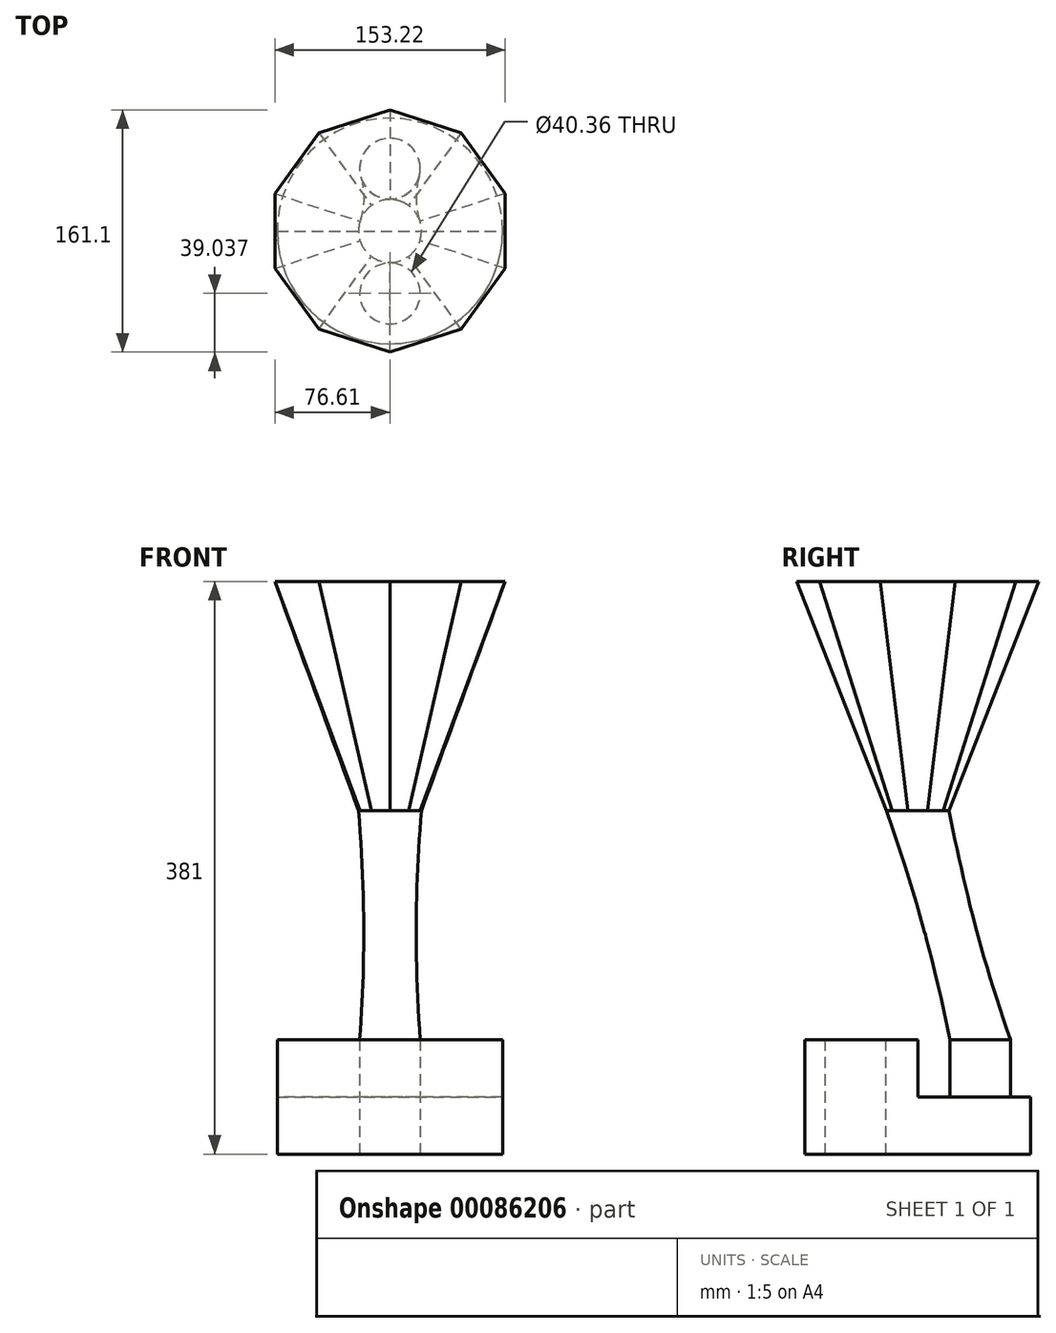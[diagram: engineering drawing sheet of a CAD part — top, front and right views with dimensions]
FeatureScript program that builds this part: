
annotation { "Feature Type Name" : "Feature", "Feature Type Description" : "" }
export const myFeature = defineFeature(function(context is Context, id is Id, definition is map)
    precondition{}
    {
        {
            var Q0;
            Q0=qCreatedBy(makeId("Top.planeOp"),FACE);
            var sketch = newSketch(context, id + "F0", { "sketchPlane" : qUnion([Q0])});
            skCircle(sketch, "E0", {"center": v(0, 0) * mm, "radius": 75.02 * mm});
            skLineSegment(sketch, "E1", {"start": v(-75.02, 0) * mm, "end": v(75.02, 0) * mm});
            skCircle(sketch, "E2", {"center": v(0, 41.51) * mm, "radius": 20.18 * mm});
            skCircle(sketch, "E3.MirrorC", {"center": v(0, -41.51) * mm, "radius": 20.18 * mm});
            skSolve(sketch);
        }
        {
            var Q0;
            {var subQ0=sQuery(id+"F0.wireOp",EDGE,"E1");Q0=makeQuery(id+"F0.imprint","IMPRINT",FACE,{"disambiguationData":[TD([[makeQuery(id+"F0.imprint","IMPRINT",EDGE,{"derivedFrom":subQ0}),1.0]])]});}
            extrude(context, id + "F1", {"entities" : qUnion([Q0]), "depth" : 38.1 * mm});
        }
        {
            var Q0;
            {var subQ0=sQuery(id+"F0.wireOp",EDGE,"E1");Q0=makeQuery(id+"F0.imprint","IMPRINT",FACE,{"disambiguationData":[TD([[makeQuery(id+"F0.imprint","IMPRINT",EDGE,{"derivedFrom":subQ0}),-1.0]])]});}
            extrude(context, id + "F2", {"entities" : qUnion([Q0]), "operationType" : NewBodyOperationType.ADD, "depth" : 25.4 * mm});
        }
        {
            var Q0;
            Q0=makeQuery(id+"F0.imprint","IMPRINT",FACE,{"disambiguationData":[TD([[makeQuery(id+"F0.imprint","IMPRINT",EDGE,{"derivedFrom":sQuery(id+"F0.wireOp",EDGE,"E3.MirrorC")}),-1.0]])]});
            var Q1;
            Q1=makeQuery(id+"F0.imprint","IMPRINT",FACE,{"disambiguationData":[TD([[makeQuery(id+"F0.imprint","IMPRINT",EDGE,{"derivedFrom":sQuery(id+"F0.wireOp",EDGE,"E2")}),1.0]])]});
            extrude(context, id + "F3", {"entities" : qUnion([Q0, Q1]), "operationType" : NewBodyOperationType.ADD, "depth" : 76.2 * mm});
        }
        {
            var Q0;
            Q0=makeQuery(id+"F3.opExtrude","CAP_FACE",FACE,{"disambiguationData":[OSD([sQuery(id+"F0.wireOp",EDGE,"E3.MirrorC")])],"isStart":false});
            cPlane(context, id + "F4", {"entities" : qUnion([Q0]), "cplaneType" : CPlaneType.OFFSET, "offset" : 152.4 * mm, "width" : 152.4 * mm, "height" : 152.4 * mm});
        }
        {
            var Q0;
            Q0=qCreatedBy(id+"F4.planeOp",FACE);
            var sketch = newSketch(context, id + "F5", { "sketchPlane" : qUnion([Q0])});
            skCircle(sketch, "E4", {"center": v(0, 0) * mm, "radius": 20.94 * mm});
            skSolve(sketch);
        }
        {
            var Q0;
            Q0=makeQuery(id+"F3.opExtrude","CAP_FACE",FACE,{"disambiguationData":[OSD([sQuery(id+"F0.wireOp",EDGE,"E2")])],"isStart":false});
            var Q1;
            Q1=makeQuery(id+"F5.imprint","IMPRINT",FACE,{"disambiguationData":[TD([[makeQuery(id+"F5.imprint","IMPRINT",EDGE,{"derivedFrom":sQuery(id+"F5.wireOp",EDGE,"E4")}),1.0]])]});
            loft(context, id + "F6", {"sheetProfilesArray" : [{ "sheetProfileEntities" : qUnion([Q0]) }, { "sheetProfileEntities" : qUnion([Q1]) }]});
        }
        {
            var Q0;
            Q0=makeQuery(id+"F6.opLoft","CAP_FACE",FACE,{"disambiguationData":[OSD([makeQuery(id+"F5.imprint","IMPRINT",FACE,{"disambiguationData":[TD([[makeQuery(id+"F5.imprint","IMPRINT",EDGE,{"derivedFrom":sQuery(id+"F5.wireOp",EDGE,"E4")}),1.0]])]})])],"isStart":true});
            cPlane(context, id + "F7", {"entities" : qUnion([Q0]), "cplaneType" : CPlaneType.OFFSET, "offset" : 152.4 * mm, "width" : 152.4 * mm, "height" : 152.4 * mm});
        }
        {
            var Q0;
            Q0=qCreatedBy(id+"F7.planeOp",FACE);
            var sketch = newSketch(context, id + "F8", { "sketchPlane" : qUnion([Q0])});
            skCircle(sketch, "E5.cCircle", {"center": v(0, 0) * mm, "radius": 76.6 * mm, "construction": true});
            skLineSegment(sketch, "E5.0", {"start": v(76.6, 24.9) * mm, "end": v(76.6, -24.9) * mm});
            skLineSegment(sketch, "E5.1", {"start": v(76.6, -24.9) * mm, "end": v(47.35, -65.17) * mm});
            skLineSegment(sketch, "E5.2", {"start": v(47.35, -65.17) * mm, "end": v(0, -80.55) * mm});
            skLineSegment(sketch, "E5.3", {"start": v(0, -80.55) * mm, "end": v(-47.35, -65.17) * mm});
            skLineSegment(sketch, "E5.4", {"start": v(-47.35, -65.17) * mm, "end": v(-76.6, -24.9) * mm});
            skLineSegment(sketch, "E5.5", {"start": v(-76.6, -24.9) * mm, "end": v(-76.6, 24.9) * mm});
            skLineSegment(sketch, "E5.6", {"start": v(-76.6, 24.9) * mm, "end": v(-47.35, 65.17) * mm});
            skLineSegment(sketch, "E5.7", {"start": v(-47.35, 65.17) * mm, "end": v(0, 80.55) * mm});
            skLineSegment(sketch, "E5.8", {"start": v(0, 80.55) * mm, "end": v(47.35, 65.17) * mm});
            skLineSegment(sketch, "E5.9", {"start": v(47.35, 65.17) * mm, "end": v(76.6, 24.9) * mm});
            skPoint(sketch, "E5.0.midPoint", {"position": v(76.6, 0) * mm});
            skSolve(sketch);
        }
        {
            var Q1;
            Q1=makeQuery(id+"F8.imprint","IMPRINT",FACE,{"disambiguationData":[TD([[makeQuery(id+"F8.imprint","IMPRINT",EDGE,{"derivedFrom":sQuery(id+"F8.wireOp",EDGE,"E5.0")}),-1.0]])]});
            var Q2;
            Q2=makeQuery(id+"F6.opLoft","CAP_FACE",FACE,{"disambiguationData":[OSD([makeQuery(id+"F5.imprint","IMPRINT",FACE,{"disambiguationData":[TD([[makeQuery(id+"F5.imprint","IMPRINT",EDGE,{"derivedFrom":sQuery(id+"F5.wireOp",EDGE,"E4")}),1.0]])]})])],"isStart":true});
            loft(context, id + "F9", {"operationType" : NewBodyOperationType.ADD, "sheetProfilesArray" : [{ "sheetProfileEntities" : qUnion([Q1]) }, { "sheetProfileEntities" : qUnion([Q2]) }]});
        }
    });
